# Revit family: Hager-Univers-IP55-D400-H1950-Cl.II-Steel_encl-ES-es
name_source: partatom
category: Equipement électrique
units: mm (PartAtom-declared; Revit-internal decimal feet)

## family parameters
Configuration du panneau = Deux colonnes, circuits au sein
Cote de connecteur circulaire = Utiliser le diamètre
Couper avec des vides une fois chargée = Non
Hôte = Face
Partagée = Non
Point de calcul de pièce = Non
Type d'élément = Tableau de raccordement

## types (11) — shared parameters
Commentaires du type = Univers
EF000003 - Tipo de montaje = EV012274 - Instalación de suelo
EF000007 - Color = EV000270 - Gris
EF000040 - Altura = 1950 mm  [stored 6.39764 ft]
EF000049 - Profundidad = 400 mm  [stored 1.31234 ft]
EF000116 - Número RAL = 7035
EF000118 - Con placa de montaje = Non
EF000266 - Número de filas = 12
EF000339 - Tipo de cubierta = EV004216 - Puerta
EF001088 - Posibilidad de extensión = Oui
EF001131 - Profundidad interna = 400 mm  [stored 1.31234 ft]
EF001596 - Material de la carcasa = EV000179 - Acero
EF001613 - Integridad del circuito = EV000494 - Ninguno
EF002950 - Anchura de unidades de división = 24
EF003532 - Adecuado para uso en exteriores = Non
EF004293 - Resistencia al impacto (IK) = EV008784 - IK10
EF005474 - Grado de protección (IP) = EV006420 - IP55
EF006306 - Con cierre = Non
EF007800 - Adecuado para la protección contra rayos = Non
EF008873 - Corriente nominal (In) = 800 A
EF009170 - Espesor del material de la caja = 2 mm  [stored 0.00656168 ft]
EF009171 - Espesor puerta/tapa = 2 mm  [stored 0.00656168 ft]
EF009212 - Versión de la cubierta = EV000116 - Cerrado
EF015940 - Tapa con alivio de sobrepresión = Non
Fabricant = Hager
HG000002 - Con puerta o tapa = Oui
HG000003 - Gama = Univers
HG000006 - Empotrado = Non
HG000023 - Caja de doble sección = Non
HG000024 - Altura de la sección inferior = 800 mm  [stored 2.62467 ft]
HG000026 - Instalación en suelo = Oui
HG000027 - Altura de zócalo = 100 mm  [stored 0.328084 ft]
zero-valued in all types: EF000218 - Profundidad de instalación, Elévation par défaut

## per-type parameters (varying)
| type | EF000008 - Anchura | EF000437 - Número de entradas de conductos de cables | EF004427 - Número de módulos | EF004464 - Tipo de puerta | EF006244 - Tapa/puerta transparente | EF009554 - Número de aberturas para placas-brida | HG000004 - Referencia del fabricante | HG000009 - Puerta batiente doble | HG000010 - Puertas asimétricas |
| Instalación de suelo IP55 A1050 A1950 P400  - FR24H1 | 1050 mm | 8 | 576 | EV003602 - Doble | Non | 8 | FR24H1 | Oui | Oui |
| Instalación de suelo IP55 A1050 A1950 P400  - FR24U1 | 1050 mm | 8 | 576 | EV003602 - Doble | Oui | 8 | FR24U1 | Oui | Oui |
| Instalación de suelo IP55 A1300 A1950 P400  - FR25H1 | 1300 mm  [stored 4.26509 ft] | 10 | 720 | EV003602 - Doble | Non | 10 | FR25H1 | Oui | Oui |
| Instalación de suelo IP55 A1300 A1950 P400  - FR25U1 | 1300 mm  [stored 4.26509 ft] | 10 | 720 | EV003602 - Doble | Oui | 10 | FR25U1 | Oui | Oui |
| Instalación de suelo IP55 A1550 A1950 P400  - FR26H1 | 1550 mm  [stored 5.0853 ft] | 12 | 864 | EV003602 - Doble | Non | 12 | FR26H1 | Oui | Oui |
| Instalación de suelo IP55 A1550 A1950 P400  - FR26U1 | 1550 mm  [stored 5.0853 ft] | 12 | 864 | EV003602 - Doble | Oui | 12 | FR26U1 | Oui | Oui |
| Instalación de suelo IP55 A300 A1950 P400  - FR21H1 | 300 mm | 2 | 144 | EV002646 - Único | Non | 2 | FR21H1 | Non | Non |
| Instalación de suelo IP55 A550 A1950 P400  - FR22H1 | 550 mm | 4 | 288 | EV002646 - Único | Non | 4 | FR22H1 | Non | Non |
| Instalación de suelo IP55 A550 A1950 P400  - FR22U1 | 550 mm | 4 | 288 | EV002646 - Único | Oui | 4 | FR22U1 | Non | Non |
| Instalación de suelo IP55 A800 A1950 P400  - FR23H1 | 800 mm  [stored 2.62467 ft] | 6 | 432 | EV002646 - Único | Non | 6 | FR23H1 | Non | Non |
| Instalación de suelo IP55 A800 A1950 P400  - FR23U1 | 800 mm  [stored 2.62467 ft] | 6 | 432 | EV002646 - Único | Oui | 6 | FR23U1 | Non | Non |

note: [stored X ft] marks values corroborated as IEEE doubles in the binary element streams (Revit-internal decimal feet)

## geometry (parser evidence)
native form markers: Sweep x10
no freeform markers — native parametric forms only
